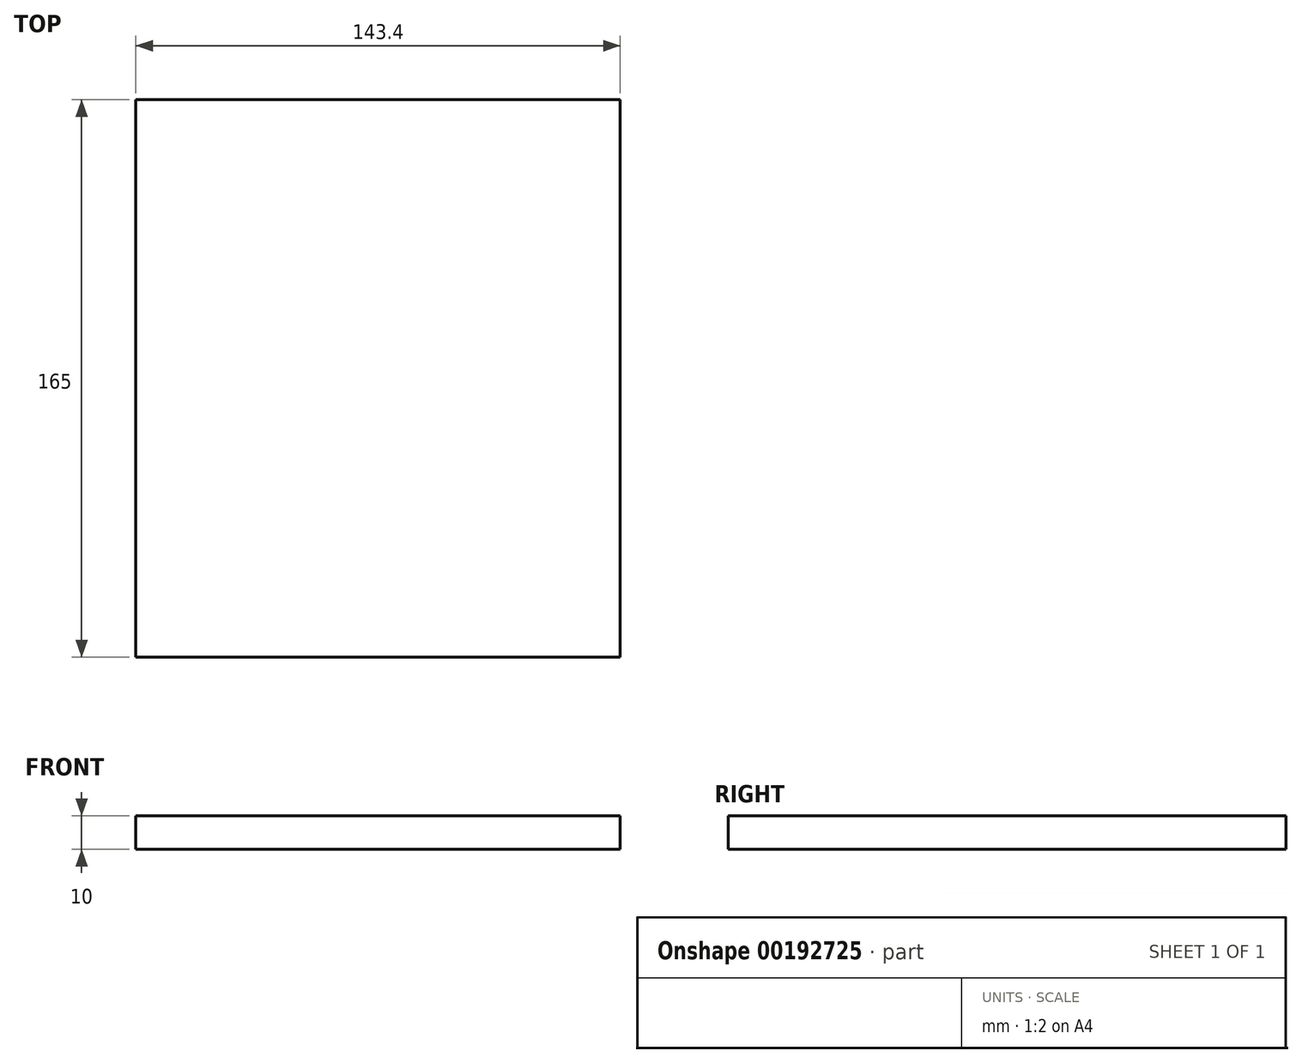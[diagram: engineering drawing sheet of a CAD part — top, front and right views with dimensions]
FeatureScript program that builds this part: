
annotation { "Feature Type Name" : "Feature", "Feature Type Description" : "" }
export const myFeature = defineFeature(function(context is Context, id is Id, definition is map)
    precondition{}
    {
        {
            var Q0;
            Q0=qCreatedBy(makeId("Top.planeOp"),FACE);
            var sketch = newSketch(context, id + "F0", { "sketchPlane" : qUnion([Q0])});
            skLineSegment(sketch, "E0.bottom", {"start": v(71.7, 82.5) * mm, "end": v(-71.7, 82.5) * mm});
            skLineSegment(sketch, "E0.top", {"start": v(71.7, -82.5) * mm, "end": v(-71.7, -82.5) * mm});
            skLineSegment(sketch, "E0.left", {"start": v(71.7, 82.5) * mm, "end": v(71.7, -82.5) * mm});
            skLineSegment(sketch, "E0.right", {"start": v(-71.7, 82.5) * mm, "end": v(-71.7, -82.5) * mm});
            skPoint(sketch, "E0.middle", {"position": v(0, 0) * mm});
            skSolve(sketch);
        }
        {
            var Q0;
            Q0 = qSketchRegion(id + "F0", true);
            extrude(context, id + "F1", {"entities" : qUnion([Q0]), "depth" : 10 * mm});
        }
    });
